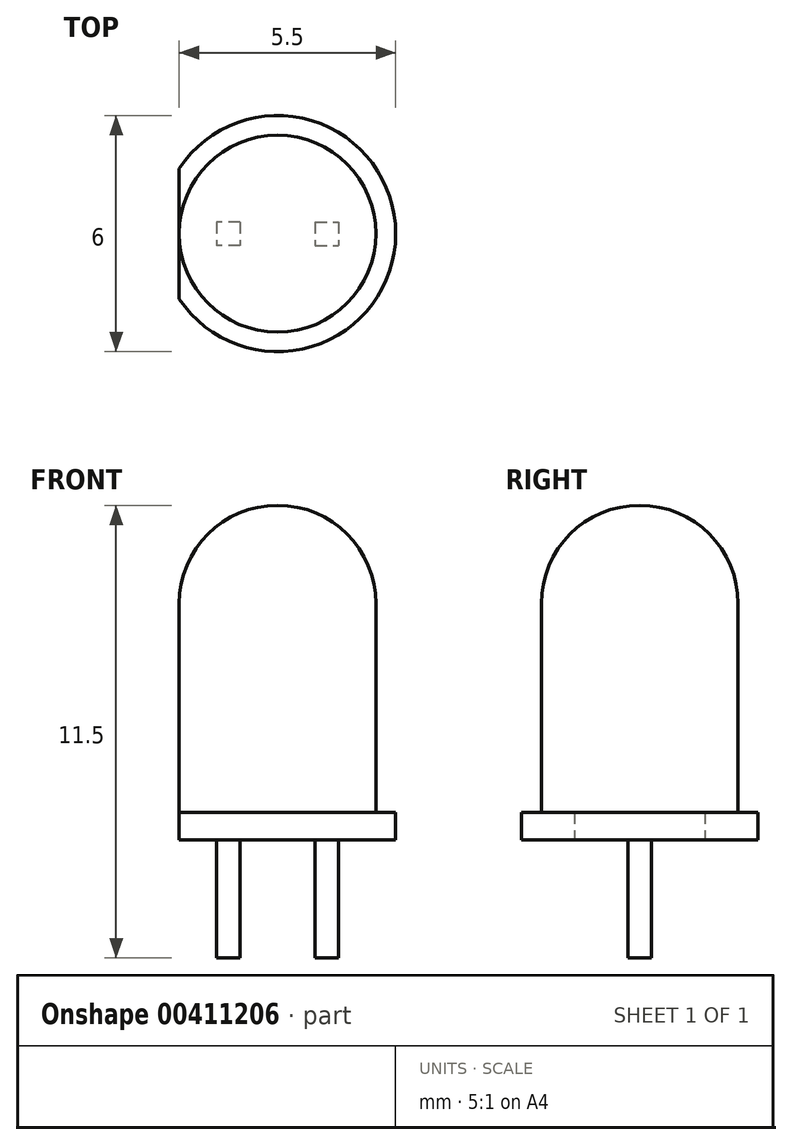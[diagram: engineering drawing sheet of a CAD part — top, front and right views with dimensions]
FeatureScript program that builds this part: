
annotation { "Feature Type Name" : "Feature", "Feature Type Description" : "" }
export const myFeature = defineFeature(function(context is Context, id is Id, definition is map)
    precondition{}
    {
        {
            var Q0;
            Q0=qCreatedBy(makeId("Top.planeOp"),FACE);
            var sketch = newSketch(context, id + "F0", { "sketchPlane" : qUnion([Q0])});
            skCircle(sketch, "E0", {"center": v(0, 0) * mm, "radius": 2.5 * mm});
            skSolve(sketch);
        }
        {
            var Q0;
            Q0=qSketchRegion(id+"F0",true);
            extrude(context, id + "F1", {"entities" : qUnion([Q0]), "depth" : 6 * mm});
        }
        {
            var Q0;
            Q0=makeQuery(id+"F1.opExtrude","CAP_FACE",FACE,{"disambiguationData":[OSD([sQuery(id+"F0.wireOp",EDGE,"E0")])],"isStart":false});
            var sketch = newSketch(context, id + "F2", { "sketchPlane" : qUnion([Q0])});
            skLineSegment(sketch, "E1", {"start": v(0, -2.5) * mm, "end": v(0, 2.5) * mm});
            skArc(sketch, "E2", {"start": v(0, 2.5) * mm, "mid": v(-2.5, 0) * mm, "end": v(0, -2.5) * mm});
            skSolve(sketch);
        }
        {
            var Q0;
            Q0=qSketchRegion(id+"F2",true);
            var Q1;
            Q1=sQuery(id+"F2.wireOp",EDGE,"E1");
            revolve(context, id + "F3", {"operationType" : NewBodyOperationType.ADD, "entities" : qUnion([Q0]), "axis" : qUnion([Q1]), "revolveType" : RevolveType.FULL});
        }
        {
            var Q0;
            Q0=makeQuery(id+"F1.opExtrude","CAP_FACE",FACE,{"disambiguationData":[OSD([sQuery(id+"F0.wireOp",EDGE,"E0")])],"isStart":true});
            var sketch = newSketch(context, id + "F4", { "sketchPlane" : qUnion([Q0])});
            skArc(sketch, "E3.0", {"start": v(-2.5, -1.66) * mm, "mid": v(3, 0) * mm, "end": v(-2.5, 1.66) * mm});
            skLineSegment(sketch, "E4", {"start": v(-2.5, -1.66) * mm, "end": v(-2.5, 1.66) * mm});
            skSolve(sketch);
        }
        {
            var Q0;
            Q0=qSketchRegion(id+"F4",true);
            extrude(context, id + "F5", {"entities" : qUnion([Q0]), "operationType" : NewBodyOperationType.ADD, "oppositeDirection" : true, "depth" : .7 * mm});
        }
        {
            var Q0;
            Q0=makeQuery(id+"F5.boolean.opBoolean","MERGE",FACE,{"derivedFrom":[makeQuery(id+"F1.opExtrude","CAP_FACE",FACE,{"disambiguationData":[OSD([sQuery(id+"F0.wireOp",EDGE,"E0")])],"isStart":true}),makeQuery(id+"F5.opExtrude","CAP_FACE",FACE,{"disambiguationData":[OSD([sQuery(id+"F4.wireOp",EDGE,"E3.0"),sQuery(id+"F4.wireOp",EDGE,"E4")])],"isStart":true})]});
            var sketch = newSketch(context, id + "F6", { "sketchPlane" : qUnion([Q0])});
            skLineSegment(sketch, "E5.rect.bottom", {"start": v(0.95, -0.3) * mm, "end": v(1.55, -0.3) * mm});
            skLineSegment(sketch, "E5.rect.top", {"start": v(0.95, 0.3) * mm, "end": v(1.55, 0.3) * mm});
            skLineSegment(sketch, "E5.rect.left", {"start": v(0.95, -0.3) * mm, "end": v(0.95, 0.3) * mm});
            skLineSegment(sketch, "E5.rect.right", {"start": v(1.55, -0.3) * mm, "end": v(1.55, 0.3) * mm});
            skPoint(sketch, "E5.rect.middle", {"position": v(1.25, 0) * mm});
            skLineSegment(sketch, "E6.rect.bottom", {"start": v(-0.95, -0.3) * mm, "end": v(-1.55, -0.3) * mm});
            skLineSegment(sketch, "E6.rect.top", {"start": v(-0.95, 0.3) * mm, "end": v(-1.55, 0.3) * mm});
            skLineSegment(sketch, "E6.rect.left", {"start": v(-0.95, -0.3) * mm, "end": v(-0.95, 0.3) * mm});
            skLineSegment(sketch, "E6.rect.right", {"start": v(-1.55, -0.3) * mm, "end": v(-1.55, 0.3) * mm});
            skPoint(sketch, "E6.rect.middle", {"position": v(-1.25, 0) * mm});
            skLineSegment(sketch, "E7", {"start": v(1.55, -0.3) * mm, "end": v(0.95, 0.3) * mm, "construction": true});
            skLineSegment(sketch, "E8", {"start": v(1.55, 0.3) * mm, "end": v(0.95, -0.3) * mm, "construction": true});
            skLineSegment(sketch, "E9", {"start": v(-0.95, -0.3) * mm, "end": v(-1.55, 0.3) * mm, "construction": true});
            skLineSegment(sketch, "E10", {"start": v(-0.95, 0.3) * mm, "end": v(-1.55, -0.3) * mm, "construction": true});
            skLineSegment(sketch, "E11", {"start": v(1.25, 0) * mm, "end": v(-1.25, 0) * mm, "construction": true});
            skSolve(sketch);
        }
        {
            var Q0;
            Q0=qSketchRegion(id+"F6",true);
            extrude(context, id + "F7", {"entities" : qUnion([Q0]), "operationType" : NewBodyOperationType.ADD, "depth" : 3 * mm});
        }
    });
